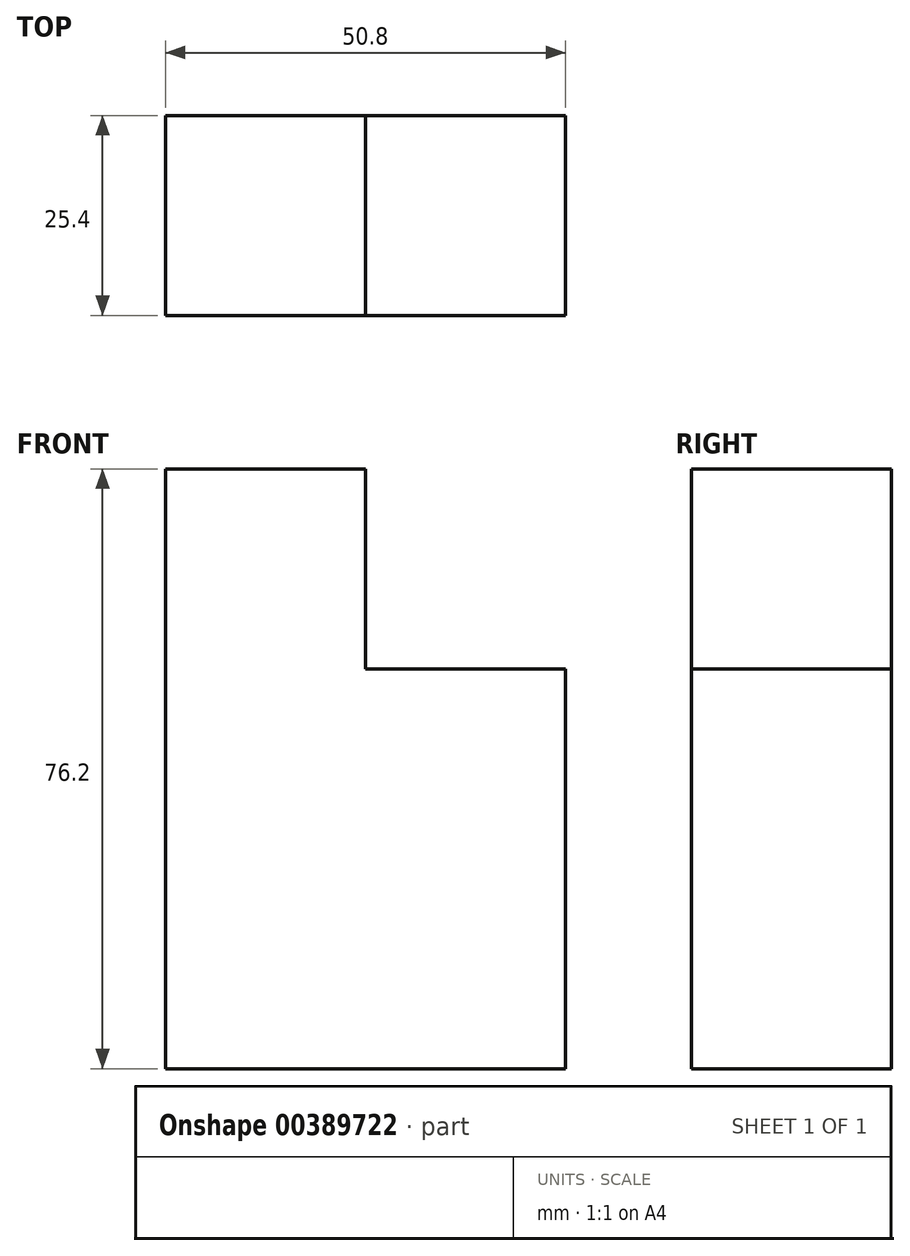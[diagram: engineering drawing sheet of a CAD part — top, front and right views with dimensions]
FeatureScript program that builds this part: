
annotation { "Feature Type Name" : "Feature", "Feature Type Description" : "" }
export const myFeature = defineFeature(function(context is Context, id is Id, definition is map)
    precondition{}
    {
        {
            var Q0;
            Q0=qCreatedBy(makeId("Front.planeOp"),FACE);
            var sketch = newSketch(context, id + "F0", { "sketchPlane" : qUnion([Q0])});
            skLineSegment(sketch, "E0.bottom", {"start": v(0, 0) * mm, "end": v(25.4, 0) * mm});
            skLineSegment(sketch, "E0.top", {"start": v(0, 25.4) * mm, "end": v(25.4, 25.4) * mm});
            skLineSegment(sketch, "E0.left", {"start": v(0, 0) * mm, "end": v(0, 25.4) * mm});
            skLineSegment(sketch, "E0.right", {"start": v(25.4, 0) * mm, "end": v(25.4, 25.4) * mm});
            skLineSegment(sketch, "E1.bottom", {"start": v(25.4, 25.4) * mm, "end": v(0, 25.4) * mm});
            skLineSegment(sketch, "E1.top", {"start": v(25.4, 50.8) * mm, "end": v(0, 50.8) * mm});
            skLineSegment(sketch, "E1.left", {"start": v(25.4, 25.4) * mm, "end": v(25.4, 50.8) * mm});
            skLineSegment(sketch, "E1.right", {"start": v(0, 25.4) * mm, "end": v(0, 50.8) * mm});
            skLineSegment(sketch, "E2.bottom", {"start": v(0, 50.8) * mm, "end": v(25.4, 50.8) * mm});
            skLineSegment(sketch, "E2.top", {"start": v(0, 76.2) * mm, "end": v(25.4, 76.2) * mm});
            skLineSegment(sketch, "E2.left", {"start": v(0, 50.8) * mm, "end": v(0, 76.2) * mm});
            skLineSegment(sketch, "E2.right", {"start": v(25.4, 50.8) * mm, "end": v(25.4, 76.2) * mm});
            skLineSegment(sketch, "E3.bottom", {"start": v(25.4, 50.8) * mm, "end": v(50.8, 50.8) * mm});
            skLineSegment(sketch, "E3.top", {"start": v(25.4, 25.4) * mm, "end": v(50.8, 25.4) * mm});
            skLineSegment(sketch, "E3.left", {"start": v(25.4, 50.8) * mm, "end": v(25.4, 25.4) * mm});
            skLineSegment(sketch, "E3.right", {"start": v(50.8, 50.8) * mm, "end": v(50.8, 25.4) * mm});
            skLineSegment(sketch, "E4.top", {"start": v(25.4, 0) * mm, "end": v(50.8, 0) * mm});
            skLineSegment(sketch, "E4.left", {"start": v(25.4, 25.4) * mm, "end": v(25.4, 0) * mm});
            skLineSegment(sketch, "E4.right", {"start": v(50.8, 25.4) * mm, "end": v(50.8, 0) * mm});
            skSolve(sketch);
        }
        {
            var Q0;
            Q0 = qSketchRegion(id + "F0", true);
            extrude(context, id + "F1", {"entities" : qUnion([Q0]), "depth" : 25.4 * mm});
        }
    });
